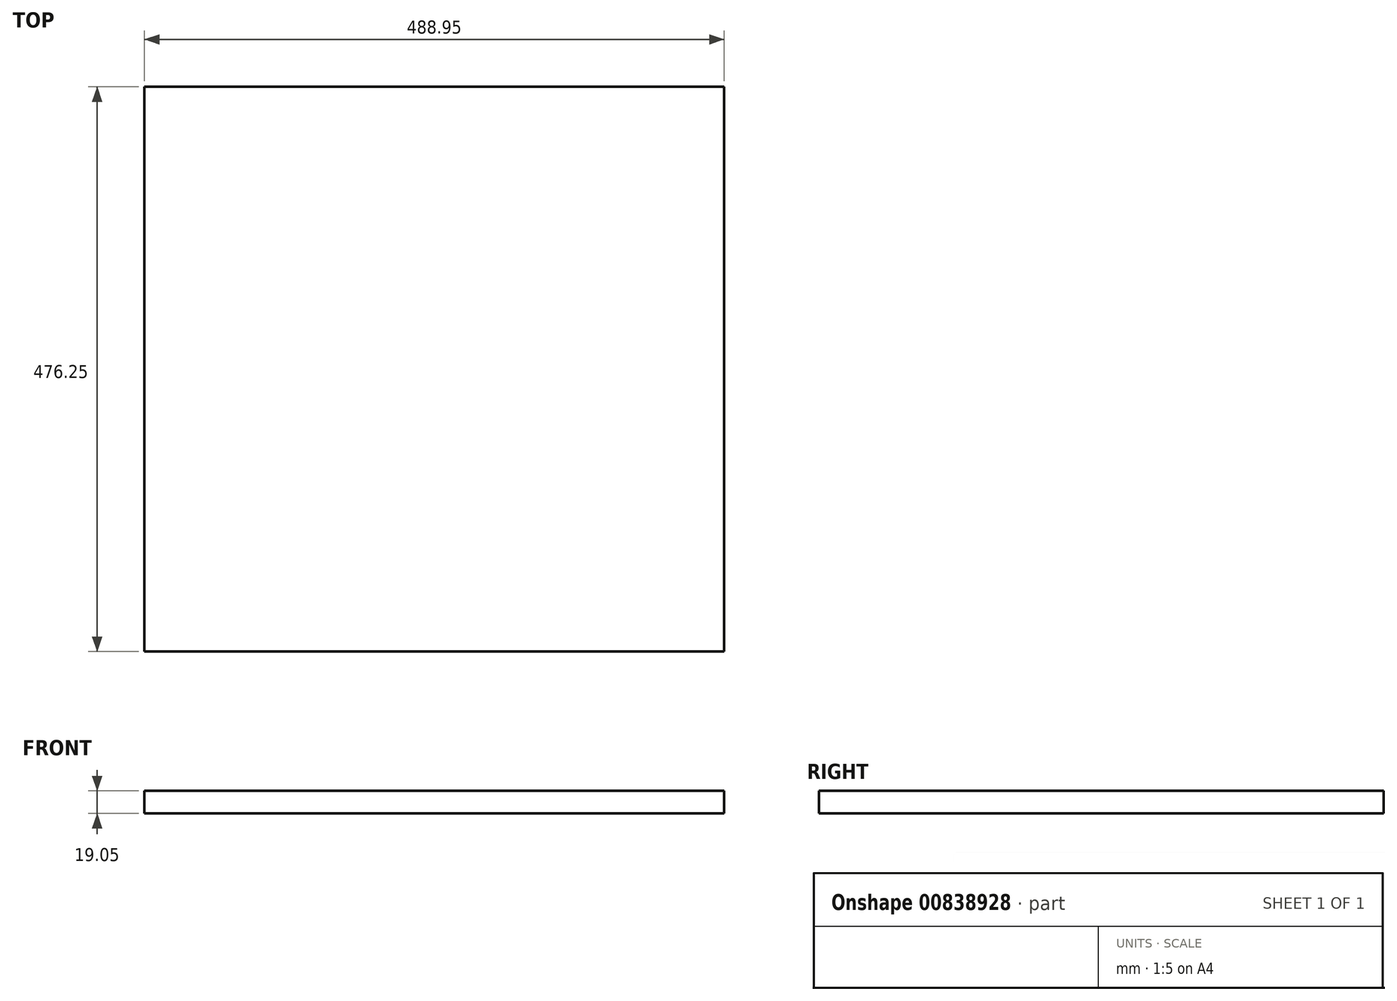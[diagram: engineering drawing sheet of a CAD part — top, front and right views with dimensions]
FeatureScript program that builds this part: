
annotation { "Feature Type Name" : "Feature", "Feature Type Description" : "" }
export const myFeature = defineFeature(function(context is Context, id is Id, definition is map)
    precondition{}
    {
        {
            var Q0;
            Q0=qCreatedBy(makeId("Right.planeOp"),FACE);
            var sketch = newSketch(context, id + "F0", { "sketchPlane" : qUnion([Q0])});
            skLineSegment(sketch, "E0", {"start": v(0, 0) * mm, "end": v(0, 19.05) * mm});
            skLineSegment(sketch, "E1", {"start": v(0, 19.05) * mm, "end": v(476.25, 19.05) * mm});
            skLineSegment(sketch, "E2", {"start": v(476.25, 19.05) * mm, "end": v(476.25, 0) * mm});
            skLineSegment(sketch, "E3", {"start": v(476.25, 0) * mm, "end": v(0, 0) * mm});
            skSolve(sketch);
        }
        {
            var Q0;
            Q0 = qSketchRegion(id + "F0", true);
            extrude(context, id + "F1", {"entities" : qUnion([Q0]), "depth" : 488.95 * mm, "offsetDistance" : 25.4 * mm});
        }
    });
